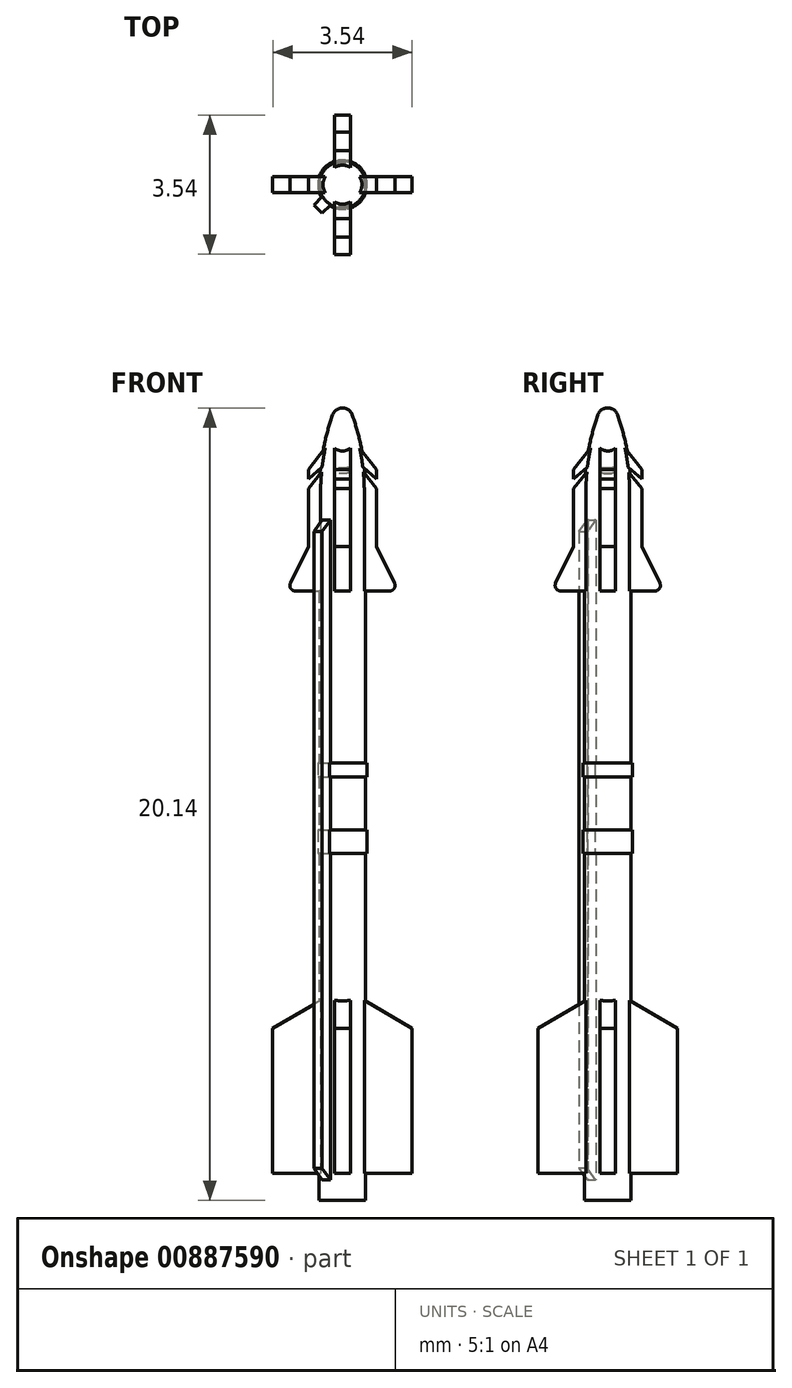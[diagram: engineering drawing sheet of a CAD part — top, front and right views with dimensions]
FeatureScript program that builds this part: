
annotation { "Feature Type Name" : "Feature", "Feature Type Description" : "" }
export const myFeature = defineFeature(function(context is Context, id is Id, definition is map)
    precondition{}
    {
        {
            assignVariable(context, id + "F0", {"name" : "s", "anyValue" : 144});
        }
        {
            var Q0;
            Q0=qCreatedBy(makeId("Front.planeOp"),FACE);
            var sketch = newSketch(context, id + "F1", { "sketchPlane" : qUnion([Q0])});
            skLineSegment(sketch, "E0", {"start": v(0, 0) * mm, "end": v(0, 20.14) * mm});
            skLineSegment(sketch, "E1", {"start": v(0.6, 17.99) * mm, "end": v(0.6, 0) * mm});
            skLineSegment(sketch, "E2", {"start": v(0.6, 0) * mm, "end": v(0, 0) * mm});
            skArc(sketch, "E3", {"start": v(0.25, 19.97) * mm, "mid": v(0.15, 20.1) * mm, "end": v(0, 20.14) * mm});
            skLineSegment(sketch, "E4", {"start": v(0, 20.14) * mm, "end": v(5.53, 20.14) * mm, "construction": true});
            skArc(sketch, "E5", {"start": v(0.6, 17.99) * mm, "mid": v(0.5, 19) * mm, "end": v(0.25, 19.97) * mm});
            skLineSegment(sketch, "E6.bottom", {"start": v(0.6, 9.4) * mm, "end": v(0.63, 9.4) * mm});
            skLineSegment(sketch, "E6.top", {"start": v(0.6, 8.82) * mm, "end": v(0.63, 8.82) * mm});
            skLineSegment(sketch, "E6.left", {"start": v(0.6, 9.4) * mm, "end": v(0.6, 8.82) * mm});
            skLineSegment(sketch, "E6.right", {"start": v(0.63, 9.4) * mm, "end": v(0.63, 8.82) * mm});
            skLineSegment(sketch, "E7.bottom", {"start": v(0.6, 11.11) * mm, "end": v(0.63, 11.11) * mm});
            skLineSegment(sketch, "E7.top", {"start": v(0.6, 10.76) * mm, "end": v(0.63, 10.76) * mm});
            skLineSegment(sketch, "E7.left", {"start": v(0.6, 11.11) * mm, "end": v(0.6, 10.76) * mm});
            skLineSegment(sketch, "E7.right", {"start": v(0.63, 11.11) * mm, "end": v(0.63, 10.76) * mm});
            skSolve(sketch);
        }
        {
            var Q0;
            {var subQ0=sQuery(id+"F1.wireOp",EDGE,"mrwio9nY-PsAZ-Zbfy-NhIU-sYq0QVbgGXAG");Q0=makeQuery(id+"F1.imprint","IMPRINT",FACE,{"disambiguationData":[TD([[makeQuery(id+"F1.imprint","IMPRINT",EDGE,{"derivedFrom":subQ0}),-1.0]])]});}
            var Q1;
            {var subQ2=sQuery(id+"F1.wireOp",EDGE,"E6.bottom");Q1=makeQuery(id+"F1.imprint","IMPRINT",FACE,{"disambiguationData":[TD([[makeQuery(id+"F1.imprint","IMPRINT",EDGE,{"derivedFrom":subQ2}),-1.0]])]});}
            var Q2;
            Q2=makeQuery(id+"F1.imprint","IMPRINT",FACE,{"disambiguationData":[TD([[makeQuery(id+"F1.imprint","IMPRINT",EDGE,{"derivedFrom":sQuery(id+"F1.wireOp",EDGE,"E0")}),-1.0]])]});
            var Q3;
            {var subQ2=sQuery(id+"F1.wireOp",EDGE,"E7.bottom");Q3=makeQuery(id+"F1.imprint","IMPRINT",FACE,{"disambiguationData":[TD([[makeQuery(id+"F1.imprint","IMPRINT",EDGE,{"derivedFrom":subQ2}),-1.0]])]});}
            var Q4;
            Q4=sQuery(id+"F1.wireOp",EDGE,"E0");
            revolve(context, id + "F2", {"surfaceOperationType" : NewSurfaceOperationType.NEW, "entities" : qUnion([Q0, Q1, Q2, Q3]), "axis" : qUnion([Q4]), "revolveType" : RevolveType.FULL});
        }
        {
            var Q0;
            Q0=qCreatedBy(makeId("Front.planeOp"),FACE);
            var sketch = newSketch(context, id + "F3", { "sketchPlane" : qUnion([Q0])});
            skLineSegment(sketch, "E8", {"start": v(0, 0) * mm, "end": v(0, 19.66) * mm});
            skLineSegment(sketch, "E9", {"start": v(0.2, 18.93) * mm, "end": v(0.87, 18.1) * mm});
            skLineSegment(sketch, "E10", {"start": v(0.87, 18.1) * mm, "end": v(0.87, 16.69) * mm});
            skLineSegment(sketch, "E11", {"start": v(0.87, 16.69) * mm, "end": v(0.2, 18.06) * mm});
            skLineSegment(sketch, "E12", {"start": v(0.2, 18.06) * mm, "end": v(0.2, 17.99) * mm});
            skLineSegment(sketch, "E13", {"start": v(0.2, 17.99) * mm, "end": v(1.32, 15.69) * mm});
            skLineSegment(sketch, "E14", {"start": v(1.2, 15.49) * mm, "end": v(0.4, 15.49) * mm});
            skLineSegment(sketch, "E15", {"start": v(0.4, 15.49) * mm, "end": v(0.4, 5.18) * mm});
            skLineSegment(sketch, "E16", {"start": v(0.4, 5.18) * mm, "end": v(1.77, 4.38) * mm});
            skLineSegment(sketch, "E17", {"start": v(1.77, 4.38) * mm, "end": v(1.77, 0.7) * mm});
            skLineSegment(sketch, "E18", {"start": v(0.6, 0) * mm, "end": v(0.6, 32.87) * mm, "construction": true});
            skPoint(sketch, "E19", {"position": v(0.6, 5.07) * mm});
            skPoint(sketch, "E20", {"position": v(0.6, 15.49) * mm});
            skPoint(sketch, "E21", {"position": v(0.6, 17.19) * mm});
            skPoint(sketch, "E22", {"position": v(0.6, 17.26) * mm});
            skPoint(sketch, "E23", {"position": v(0.6, 18.44) * mm});
            skLineSegment(sketch, "E24", {"start": v(1.77, 0.7) * mm, "end": v(0, 0.7) * mm});
            skLineSegment(sketch, "E25.0", {"start": v(0.6, 0) * mm, "end": v(-0.6, 0) * mm});
            skPoint(sketch, "E26.visualSharp", {"position": v(1.42, 15.49) * mm});
            skArc(sketch, "E26.filletArc", {"start": v(1.2, 15.49) * mm, "mid": v(1.32, 15.55) * mm, "end": v(1.32, 15.69) * mm});
            skLineSegment(sketch, "E27", {"start": v(0.87, 16.69) * mm, "end": v(0.87, 16.62) * mm});
            skLineSegment(sketch, "E28", {"start": v(0.2, 18.92) * mm, "end": v(0.2, 18.93) * mm});
            skLineSegment(sketch, "E29", {"start": v(0.2, 18.92) * mm, "end": v(0.87, 18.33) * mm});
            skLineSegment(sketch, "E30", {"start": v(0.87, 18.33) * mm, "end": v(0.87, 18.58) * mm});
            skLineSegment(sketch, "E31", {"start": v(0.87, 18.58) * mm, "end": v(0, 19.66) * mm});
            skPoint(sketch, "E32", {"position": v(0.6, 18.58) * mm});
            skPoint(sketch, "E33", {"position": v(0.6, 18.92) * mm});
            skSolve(sketch);
        }
        {
            var Q0;
            Q0=qSketchRegion(id+"F3",true);
            extrude(context, id + "F4", {"entities" : qUnion([Q0]), "operationType" : NewBodyOperationType.ADD, "depth" : .4 * mm, "offsetDistance" : 25 * mm, "symmetric" : true});
        }
        {
            var Q0;
            Q0=makeQuery(id+"F2.opRevolve","SWEPT_BODY",BODY,{"disambiguationData":[OSD([sQuery(id+"F1.wireOp",EDGE,"E0"),sQuery(id+"F1.wireOp",EDGE,"E1"),sQuery(id+"F1.wireOp",EDGE,"E2"),sQuery(id+"F1.wireOp",EDGE,"E3"),sQuery(id+"F1.wireOp",EDGE,"E5"),sQuery(id+"F1.wireOp",EDGE,"E6.bottom"),sQuery(id+"F1.wireOp",EDGE,"E6.top"),sQuery(id+"F1.wireOp",EDGE,"E6.right"),sQuery(id+"F1.wireOp",EDGE,"E7.bottom"),sQuery(id+"F1.wireOp",EDGE,"E7.top"),sQuery(id+"F1.wireOp",EDGE,"E7.right")])]});
            var Q1;
            Q1=makeQuery(id+"F2.opRevolve","SWEPT_FACE",FACE,{"disambiguationData":[OSD([sQuery(id+"F1.wireOp",EDGE,"E6.right")])]});
            circularPattern(context, id + "F5", {"operationType" : NewBodyOperationType.ADD, "entities" : qUnion([Q0]), "axis" : qUnion([Q1]), "angle" : 360 * degree, "instanceCount" : 4, "equalSpace" : true, "computeTransformsWithoutBuiltin" : true});
        }
        {
            var Q0;
            Q0=qCreatedBy(makeId("Top.planeOp"),FACE);
            cPlane(context, id + "F6", {"entities" : qUnion([Q0]), "cplaneType" : CPlaneType.OFFSET, "offset" : (75 / getVariable(context, 's')) * mm, "width" : 150 * mm, "height" : 150 * mm});
        }
        {
            var Q0;
            Q0=qCreatedBy(id+"F6.planeOp",FACE);
            var sketch = newSketch(context, id + "F7", { "sketchPlane" : qUnion([Q0])});
            skLineSegment(sketch, "E34", {"start": v(-0.05, -0.26) * mm, "end": v(-0.26, -0.05) * mm});
            skLineSegment(sketch, "E35", {"start": v(-0.26, -0.05) * mm, "end": v(-0.73, -0.52) * mm});
            skLineSegment(sketch, "E36", {"start": v(-0.52, -0.73) * mm, "end": v(-0.05, -0.26) * mm});
            skLineSegment(sketch, "E37", {"start": v(0, -0.45) * mm, "end": v(0, 0) * mm, "construction": true});
            skLineSegment(sketch, "E38", {"start": v(0, 0) * mm, "end": v(-0.16, -0.16) * mm, "construction": true});
            skLineSegment(sketch, "E39", {"start": v(-0.52, -0.73) * mm, "end": v(-0.73, -0.52) * mm});
            skSolve(sketch);
        }
        {
            var Q0;
            Q0=qSketchRegion(id+"F7",true);
            extrude(context, id + "F8", {"entities" : qUnion([Q0]), "operationType" : NewBodyOperationType.ADD, "depth" : (2415 / getVariable(context, 's')) * mm, "offsetDistance" : 25 * mm});
        }
        {
            var Q0;
            Q0=makeQuery(id+"F8.opExtrude","CAP_EDGE",EDGE,{"disambiguationData":[OSD([sQuery(id+"F7.wireOp",EDGE,"E39")])],"isStart":true});
            var Q1;
            Q1=makeQuery(id+"F8.opExtrude","CAP_EDGE",EDGE,{"disambiguationData":[OSD([sQuery(id+"F7.wireOp",EDGE,"E39")])],"isStart":false});
            chamfer(context, id + "F9", {"entities" : qUnion([Q0, Q1]), "width" : .3 * mm, "tangentPropagation" : true});
        }
    });
